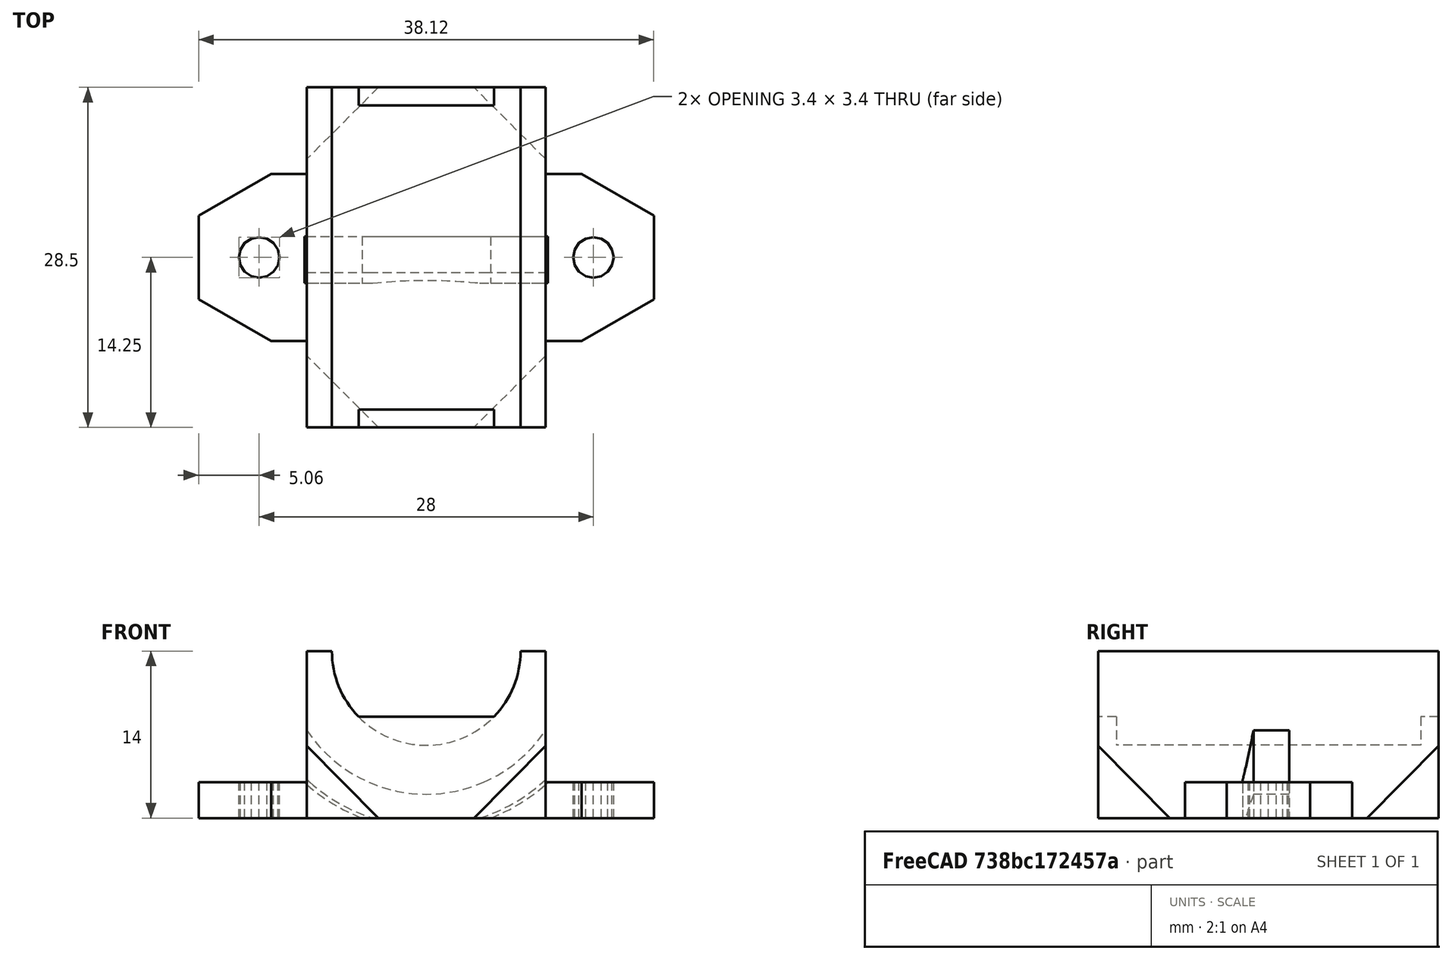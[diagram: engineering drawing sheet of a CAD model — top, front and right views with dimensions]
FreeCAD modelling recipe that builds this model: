
FCSTD DOCUMENT  (FreeCAD 0.19R)
Label: y-LM8UU-holder
License: All rights reserved
LicenseURL: http://en.wikipedia.org/wiki/All_rights_reserved
objects: Part::Box×9, Part::Cut×6, Part::Cylinder×5, Part::Fuse×5, Part::Prism×4, Part::MultiFuse×4, Part::Cone×2, Part::Mirroring×1
note: 36 computed .brp shape members not serialized (recipe doc carries the construction recipe); baked Part::Feature solids carry a one-line shape summary decoded from their .brp

FEATURE [Part::Box] cube
  AttacherType = Attacher::AttachEngine3D
  Height = 3
  Length = 26
  Placement = pos=(-13,-7,0) rot=(0,0,1;0rad)
  Width = 14
FEATURE [Part::Prism] prism
  AttacherType = Attacher::AttachEngine3D
  Circumradius = 7
  Height = 3
  Placement = pos=(-13,0,0) rot=(0,0,1;0.523599rad)
  Polygon = 6
FEATURE [Part::Prism] prism001
  AttacherType = Attacher::AttachEngine3D
  Circumradius = 7
  Height = 3
  Placement = pos=(13,0,0) rot=(0,0,1;0.523599rad)
  Polygon = 6
FEATURE [Part::MultiFuse] union
  Shapes = -> [cube,prism,prism001]
FEATURE [Part::Prism] prism002
  AttacherType = Attacher::AttachEngine3D
  Circumradius = 1.7
  Height = 10
  Placement = pos=(-14,0,-0.1) rot=(0,0,1;0rad)
  Polygon = 16
FEATURE [Part::Prism] prism003
  AttacherType = Attacher::AttachEngine3D
  Circumradius = 1.7
  Height = 10
  Placement = pos=(14,0,-0.1) rot=(0,0,1;0rad)
  Polygon = 16
FEATURE [Part::Cylinder] cylinder
  Angle = 360
  AttacherType = Attacher::AttachEngine3D
  Height = 3.9
  Radius = 15
FEATURE [Part::Cylinder] cylinder001
  Angle = 360
  AttacherType = Attacher::AttachEngine3D
  Height = 5
  Radius = 12
FEATURE [Part::Cone] cylinder002
  Angle = 360
  AttacherType = Attacher::AttachEngine3D
  Height = 1
  Placement = pos=(0,0,3) rot=(0,0,1;0rad)
  Radius1 = 12
  Radius2 = 15
FEATURE [Part::Fuse] union001
  Base = -> cylinder001
  Tool = -> cylinder002
FEATURE [Part::Cut] difference
  Base = -> cylinder
  Placement = pos=(0,1.75,14) rot=(0.57735,-0.57735,0.57735;2.0944rad)
  Tool = -> union001
FEATURE [Part::MultiFuse] union002
  Shapes = -> [prism002,prism003,difference]
FEATURE [Part::Cut] difference001
  Base = -> union
  Tool = -> union002
FEATURE [Part::Box] cube001
  AttacherType = Attacher::AttachEngine3D
  Height = 28.5
  Length = 10
  Placement = pos=(-10,-10,0) rot=(0,0,1;0rad)
  Width = 20
FEATURE [Part::Cylinder] cylinder003
  Angle = 360
  AttacherType = Attacher::AttachEngine3D
  Height = 32.5
  Placement = pos=(0,0,-2) rot=(0,0,1;0rad)
  Radius = 7.9
FEATURE [Part::Cut] difference002
  Base = -> cube001
  Tool = -> cylinder003
FEATURE [Part::Box] cube002
  AttacherType = Attacher::AttachEngine3D
  Height = 28.5
  Length = 4
  Placement = pos=(-14,-10,0) rot=(0,0,1;0rad)
  Width = 20
FEATURE [Part::Fuse] union003
  Base = -> difference002
  Tool = -> cube002
FEATURE [Part::Cylinder] cylinder004
  Angle = 360
  AttacherType = Attacher::AttachEngine3D
  Height = 3.9
  Radius = 15
FEATURE [Part::Cylinder] cylinder005
  Angle = 360
  AttacherType = Attacher::AttachEngine3D
  Height = 5
  Radius = 12
FEATURE [Part::Cone] cylinder006
  Angle = 360
  AttacherType = Attacher::AttachEngine3D
  Height = 1
  Placement = pos=(0,0,3) rot=(0,0,1;0rad)
  Radius1 = 12
  Radius2 = 15
FEATURE [Part::Fuse] union004
  Base = -> cylinder005
  Tool = -> cylinder006
FEATURE [Part::Cut] difference003
  Base = -> cylinder004
  Placement = pos=(0,0,12.5) rot=(0,0,1;0rad)
  Tool = -> union004
FEATURE [Part::Cut] difference004
  Base = -> union003
  Tool = -> difference003
FEATURE [Part::Box] cube003
  AttacherType = Attacher::AttachEngine3D
  Height = 1.5
  Length = 4.5
  Placement = pos=(-10,-10,0) rot=(0,0,1;0rad)
  Width = 20
FEATURE [Part::Box] cube004
  AttacherType = Attacher::AttachEngine3D
  Height = 1.5
  Length = 4.5
  Placement = pos=(-10,-10,27) rot=(0,0,1;0rad)
  Width = 20
FEATURE [Part::MultiFuse] Matrix_Union
  Placement = pos=(0,14.25,14) rot=(0.57735,-0.57735,0.57735;2.0944rad)
  Shapes = -> [difference004,cube003,cube004]
FEATURE [Part::Box] cube005
  AttacherType = Attacher::AttachEngine3D
  Height = 20
  Length = 20
  Placement = pos=(1.66541,-20.0575,-13.9273) rot=(0.587481,0.243343,0.771784;0.985144rad)
  Width = 10
FEATURE [Part::Box] cube006
  AttacherType = Attacher::AttachEngine3D
  Height = 20
  Length = 20
  Placement = pos=(-15.8075,-5.91541,-13.9273) rot=(0.587481,-0.243343,-0.771784;0.985144rad)
  Width = 10
FEATURE [Part::Box] cube007
  AttacherType = Attacher::AttachEngine3D
  Height = 20
  Length = 20
  Placement = pos=(1.66541,-20.0575,-13.9273) rot=(0.587481,0.243343,0.771784;0.985144rad)
  Width = 10
FEATURE [Part::Box] cube008
  AttacherType = Attacher::AttachEngine3D
  Height = 20
  Length = 20
  Placement = pos=(-15.8075,-5.91541,-13.9273) rot=(0.587481,-0.243343,-0.771784;0.985144rad)
  Width = 10
FEATURE [Part::Fuse] Matrix_Union001
  Base = -> cube007
  Tool = -> cube008
FEATURE [Part::Mirroring] mirr_Matrix_Union001  label="mirrored Matrix_Union001"
  Base = (0,0,0)
  Normal = (0,1,0)
  Source = -> Matrix_Union001
FEATURE [Part::MultiFuse] union005
  Shapes = -> [cube005,cube006,mirr_Matrix_Union001]
FEATURE [Part::Cut] difference005
  Base = -> Matrix_Union
  Tool = -> union005
FEATURE [Part::Fuse] Group
  Base = -> difference001
  Refine = true
  Tool = -> difference005
